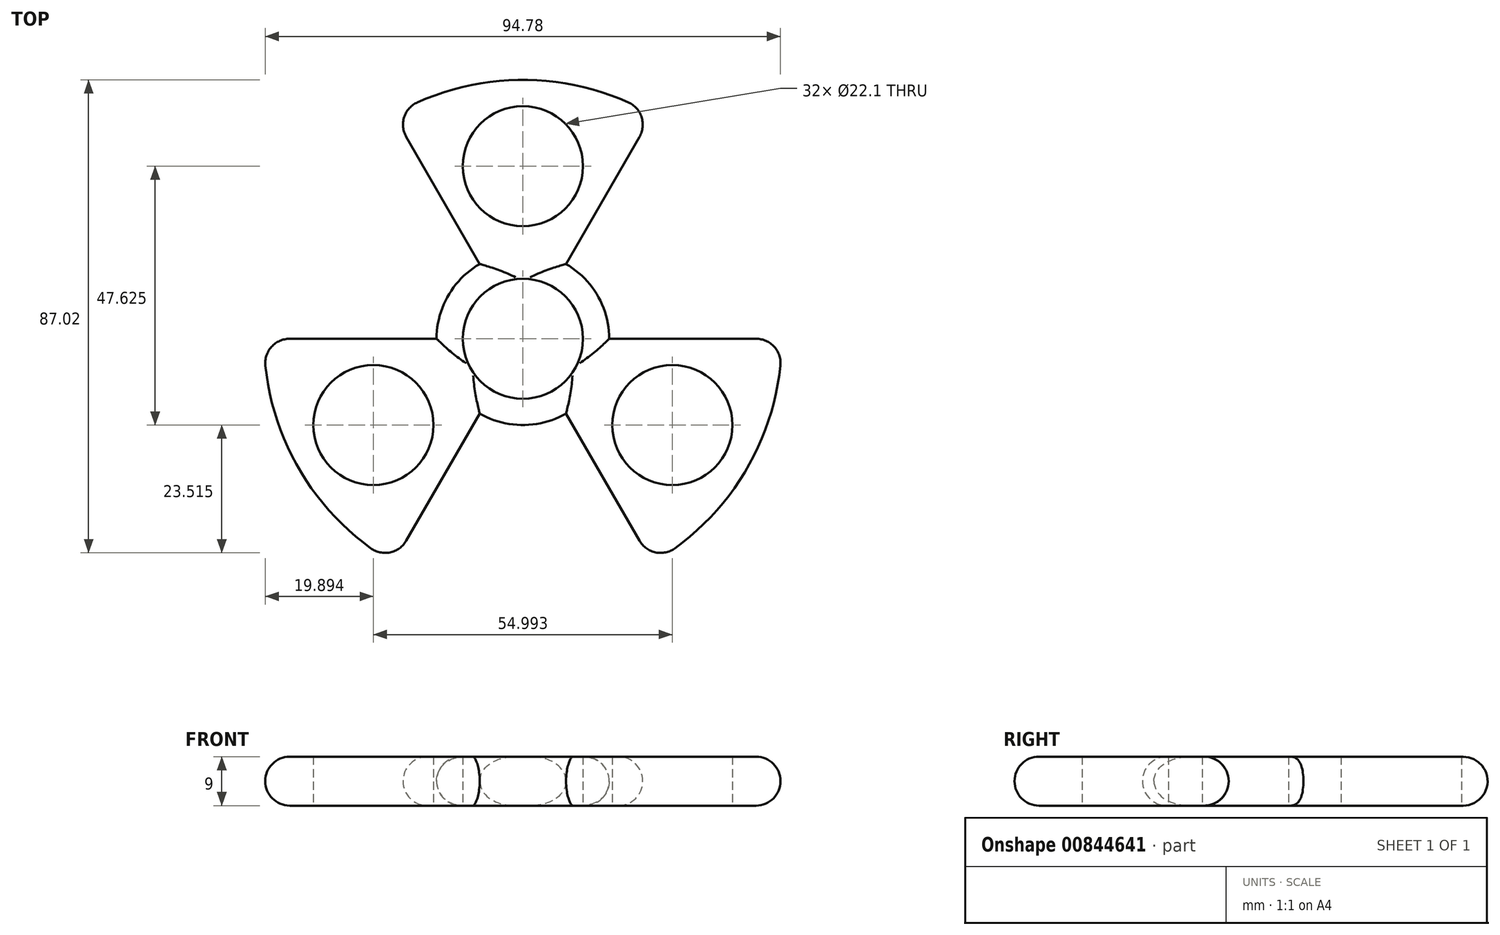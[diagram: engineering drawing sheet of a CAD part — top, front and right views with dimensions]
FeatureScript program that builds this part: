
annotation { "Feature Type Name" : "Feature", "Feature Type Description" : "" }
export const myFeature = defineFeature(function(context is Context, id is Id, definition is map)
    precondition{}
    {
        {
            var Q0;
            Q0=qCreatedBy(makeId("Top.planeOp"),FACE);
            var sketch = newSketch(context, id + "F0", { "sketchPlane" : qUnion([Q0])});
            skCircle(sketch, "E0", {"center": v(0, 0) * mm, "radius": 11.05 * mm});
            skCircle(sketch, "E1", {"center": v(0, 31.75) * mm, "radius": 11.05 * mm});
            skCircle(sketch, "E2.1.0", {"center": v(-27.5, -15.87) * mm, "radius": 11.05 * mm});
            skCircle(sketch, "E2.2.0", {"center": v(27.5, -15.88) * mm, "radius": 11.05 * mm});
            skArc(sketch, "E3", {"start": v(23.81, 41.24) * mm, "mid": v(0, 47.63) * mm, "end": v(-23.81, 41.24) * mm});
            skCircle(sketch, "E4", {"center": v(0, 0) * mm, "radius": 15.88 * mm});
            skLineSegment(sketch, "E5", {"start": v(-7.94, 13.75) * mm, "end": v(-23.81, 41.24) * mm});
            skLineSegment(sketch, "E6", {"start": v(7.94, 13.75) * mm, "end": v(23.81, 41.24) * mm});
            skLineSegment(sketch, "E7.1.0", {"start": v(-7.94, -13.75) * mm, "end": v(-23.81, -41.24) * mm});
            skArc(sketch, "E7.1.1", {"start": v(-47.63, 0) * mm, "mid": v(-41.24, -23.81) * mm, "end": v(-23.81, -41.24) * mm});
            skLineSegment(sketch, "E7.1.2", {"start": v(-15.88, 0) * mm, "end": v(-47.63, 0) * mm});
            skLineSegment(sketch, "E7.2.0", {"start": v(15.88, 0) * mm, "end": v(47.63, 0) * mm});
            skArc(sketch, "E7.2.1", {"start": v(23.81, -41.24) * mm, "mid": v(41.24, -23.81) * mm, "end": v(47.62, 0) * mm});
            skLineSegment(sketch, "E7.2.2", {"start": v(7.94, -13.75) * mm, "end": v(23.81, -41.24) * mm});
            skSolve(sketch);
        }
        {
            var Q0;
            Q0=makeQuery(id+"F0.imprint","IMPRINT",FACE,{"disambiguationData":[TD([[makeQuery(id+"F0.imprint","IMPRINT",EDGE,{"derivedFrom":sQuery(id+"F0.wireOp",EDGE,"E2.1.0")}),-1.0]])]});
            var Q1;
            Q1=makeQuery(id+"F0.imprint","IMPRINT",FACE,{"disambiguationData":[TD([[makeQuery(id+"F0.imprint","IMPRINT",EDGE,{"derivedFrom":sQuery(id+"F0.wireOp",EDGE,"E0")}),-1.0]])]});
            var Q2;
            Q2=makeQuery(id+"F0.imprint","IMPRINT",FACE,{"disambiguationData":[TD([[makeQuery(id+"F0.imprint","IMPRINT",EDGE,{"derivedFrom":sQuery(id+"F0.wireOp",EDGE,"E2.2.0")}),-1.0]])]});
            var Q3;
            Q3=makeQuery(id+"F0.imprint","IMPRINT",FACE,{"disambiguationData":[TD([[makeQuery(id+"F0.imprint","IMPRINT",EDGE,{"derivedFrom":sQuery(id+"F0.wireOp",EDGE,"E1")}),-1.0]])]});
            extrude(context, id + "F1", {"entities" : qUnion([Q0, Q1, Q2, Q3]), "depth" : 9 * mm, "offsetDistance" : 25.4 * mm});
        }
        {
            var Q0;
            Q0=makeQuery(id+"F1.opExtrude","CAP_EDGE",EDGE,{"disambiguationData":[OSD([sQuery(id+"F0.wireOp",EDGE,"E7.2.0")])],"isStart":false});
            var Q1;
            Q1=makeQuery(id+"F1.opExtrude","CAP_EDGE",EDGE,{"disambiguationData":[OSD([sQuery(id+"F0.wireOp",EDGE,"E7.2.0")])],"isStart":true});
            var Q2;
            Q2=makeQuery(id+"F1.opExtrude","CAP_EDGE",EDGE,{"disambiguationData":[OSD([sQuery(id+"F0.wireOp",EDGE,"E6")])],"isStart":false});
            var Q3;
            Q3=makeQuery(id+"F1.opExtrude","CAP_EDGE",EDGE,{"disambiguationData":[OSD([sQuery(id+"F0.wireOp",EDGE,"E6")])],"isStart":true});
            var Q4;
            Q4=makeQuery(id+"F1.opExtrude","CAP_EDGE",EDGE,{"disambiguationData":[OSD([sQuery(id+"F0.wireOp",EDGE,"E7.1.0")])],"isStart":false});
            var Q5;
            Q5=makeQuery(id+"F1.opExtrude","CAP_EDGE",EDGE,{"disambiguationData":[OSD([sQuery(id+"F0.wireOp",EDGE,"E7.1.0")])],"isStart":true});
            var Q6;
            Q6=makeQuery(id+"F1.opExtrude","CAP_EDGE",EDGE,{"disambiguationData":[OSD([sQuery(id+"F0.wireOp",EDGE,"E7.1.2")])],"isStart":false});
            var Q7;
            Q7=makeQuery(id+"F1.opExtrude","CAP_EDGE",EDGE,{"disambiguationData":[OSD([sQuery(id+"F0.wireOp",EDGE,"E7.1.2")])],"isStart":true});
            var Q8;
            Q8=makeQuery(id+"F1.opExtrude","CAP_EDGE",EDGE,{"disambiguationData":[OSD([sQuery(id+"F0.wireOp",EDGE,"E5")])],"isStart":false});
            var Q9;
            Q9=makeQuery(id+"F1.opExtrude","CAP_EDGE",EDGE,{"disambiguationData":[OSD([sQuery(id+"F0.wireOp",EDGE,"E5")])],"isStart":true});
            var Q10;
            Q10=makeQuery(id+"F1.opExtrude","CAP_EDGE",EDGE,{"disambiguationData":[OSD([sQuery(id+"F0.wireOp",EDGE,"E7.2.2")])],"isStart":true});
            var Q11;
            Q11=makeQuery(id+"F1.opExtrude","CAP_EDGE",EDGE,{"disambiguationData":[OSD([sQuery(id+"F0.wireOp",EDGE,"E7.2.2")])],"isStart":false});
            fillet(context, id + "F2", {"entities" : qUnion([Q0, Q1, Q2, Q3, Q4, Q5, Q6, Q7, Q8, Q9, Q10, Q11]), "radius" : 4.5 * mm, "tangentPropagation" : true, "allowEdgeOverflow" : false});
        }
        {
            var Q0;
            {var subQ0=sQuery(id+"F0.wireOp",EDGE,"E4");Q0=makeQuery(id+"F1.opExtrude","CAP_EDGE",EDGE,{"disambiguationData":[OSD([subQ0]),TDD([makeQuery(id+"F0.imprint","IMPRINT",EDGE,{"disambiguationData":[TD([[makeQuery(id+"F0.imprint","INTERSECT",VERTEX,{"derivedFrom":[subQ0,sQuery(id+"F0.wireOp",EDGE,"E5")]}),-1.0]])],"derivedFrom":subQ0})])],"isStart":false});}
            var Q1;
            {var subQ0=sQuery(id+"F0.wireOp",EDGE,"E4");Q1=makeQuery(id+"F1.opExtrude","CAP_EDGE",EDGE,{"disambiguationData":[OSD([subQ0]),TDD([makeQuery(id+"F0.imprint","IMPRINT",EDGE,{"disambiguationData":[TD([[makeQuery(id+"F0.imprint","INTERSECT",VERTEX,{"derivedFrom":[subQ0,sQuery(id+"F0.wireOp",EDGE,"E7.1.0")]}),-1.0]])],"derivedFrom":subQ0})])],"isStart":false});}
            var Q2;
            {var subQ0=sQuery(id+"F0.wireOp",EDGE,"E4");Q2=makeQuery(id+"F1.opExtrude","CAP_EDGE",EDGE,{"disambiguationData":[OSD([subQ0]),TDD([makeQuery(id+"F0.imprint","IMPRINT",EDGE,{"disambiguationData":[TD([[makeQuery(id+"F0.imprint","INTERSECT",VERTEX,{"derivedFrom":[subQ0,sQuery(id+"F0.wireOp",EDGE,"E6")]}),1.0]])],"derivedFrom":subQ0})])],"isStart":false});}
            var Q3;
            {var subQ0=sQuery(id+"F0.wireOp",EDGE,"E4");Q3=makeQuery(id+"F1.opExtrude","CAP_EDGE",EDGE,{"disambiguationData":[OSD([subQ0]),TDD([makeQuery(id+"F0.imprint","IMPRINT",EDGE,{"disambiguationData":[TD([[makeQuery(id+"F0.imprint","INTERSECT",VERTEX,{"derivedFrom":[subQ0,sQuery(id+"F0.wireOp",EDGE,"E6")]}),1.0]])],"derivedFrom":subQ0})])],"isStart":true});}
            var Q4;
            {var subQ0=sQuery(id+"F0.wireOp",EDGE,"E4");Q4=makeQuery(id+"F1.opExtrude","CAP_EDGE",EDGE,{"disambiguationData":[OSD([subQ0]),TDD([makeQuery(id+"F0.imprint","IMPRINT",EDGE,{"disambiguationData":[TD([[makeQuery(id+"F0.imprint","INTERSECT",VERTEX,{"derivedFrom":[subQ0,sQuery(id+"F0.wireOp",EDGE,"E5")]}),-1.0]])],"derivedFrom":subQ0})])],"isStart":true});}
            var Q5;
            {var subQ0=sQuery(id+"F0.wireOp",EDGE,"E4");Q5=makeQuery(id+"F1.opExtrude","CAP_EDGE",EDGE,{"disambiguationData":[OSD([subQ0]),TDD([makeQuery(id+"F0.imprint","IMPRINT",EDGE,{"disambiguationData":[TD([[makeQuery(id+"F0.imprint","INTERSECT",VERTEX,{"derivedFrom":[subQ0,sQuery(id+"F0.wireOp",EDGE,"E7.1.0")]}),-1.0]])],"derivedFrom":subQ0})])],"isStart":true});}
            fillet(context, id + "F3", {"entities" : qUnion([Q0, Q1, Q2, Q3, Q4, Q5]), "radius" : 4.5 * mm, "tangentPropagation" : true, "allowEdgeOverflow" : false});
        }
        {
            var Q0;
            Q0=makeQuery(id+"F1.opExtrude","CAP_EDGE",EDGE,{"disambiguationData":[OSD([sQuery(id+"F0.wireOp",EDGE,"E7.1.1")])],"isStart":false});
            var Q1;
            Q1=makeQuery(id+"F1.opExtrude","CAP_EDGE",EDGE,{"disambiguationData":[OSD([sQuery(id+"F0.wireOp",EDGE,"E7.1.1")])],"isStart":true});
            fillet(context, id + "F4", {"entities" : qUnion([Q0, Q1]), "radius" : 4.5 * mm, "tangentPropagation" : true, "allowEdgeOverflow" : false});
        }
        {
            var Q0;
            Q0=makeQuery(id+"F1.opExtrude","CAP_EDGE",EDGE,{"disambiguationData":[OSD([sQuery(id+"F0.wireOp",EDGE,"E3")])],"isStart":false});
            var Q1;
            Q1=makeQuery(id+"F1.opExtrude","CAP_EDGE",EDGE,{"disambiguationData":[OSD([sQuery(id+"F0.wireOp",EDGE,"E3")])],"isStart":true});
            var Q2;
            Q2=makeQuery(id+"F1.opExtrude","CAP_EDGE",EDGE,{"disambiguationData":[OSD([sQuery(id+"F0.wireOp",EDGE,"E7.2.1")])],"isStart":true});
            var Q3;
            Q3=makeQuery(id+"F1.opExtrude","CAP_EDGE",EDGE,{"disambiguationData":[OSD([sQuery(id+"F0.wireOp",EDGE,"E7.2.1")])],"isStart":false});
            fillet(context, id + "F5", {"entities" : qUnion([Q0, Q1, Q2, Q3]), "radius" : 4.5 * mm, "tangentPropagation" : true, "allowEdgeOverflow" : false});
        }
    });
